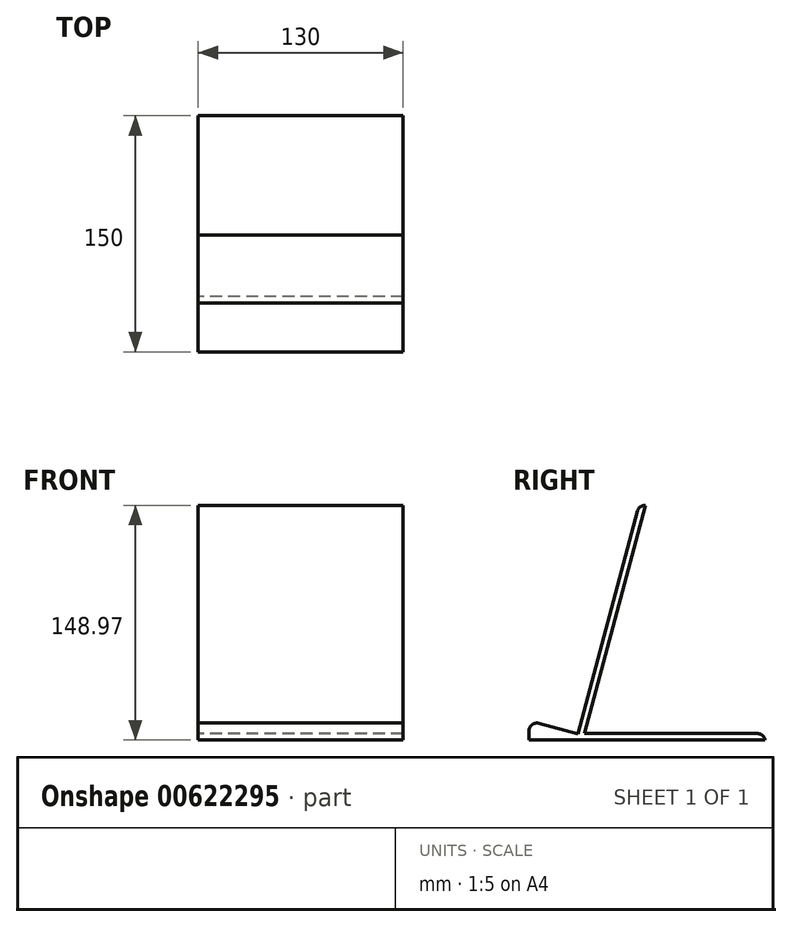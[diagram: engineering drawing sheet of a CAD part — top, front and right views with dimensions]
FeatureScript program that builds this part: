
annotation { "Feature Type Name" : "Feature", "Feature Type Description" : "" }
export const myFeature = defineFeature(function(context is Context, id is Id, definition is map)
    precondition{}
    {
        {
            var Q0;
            Q0=qCreatedBy(makeId("Right.planeOp"),FACE);
            var sketch = newSketch(context, id + "F0", { "sketchPlane" : qUnion([Q0])});
            skLineSegment(sketch, "E0", {"start": v(0, 0) * mm, "end": v(120, 0) * mm});
            skLineSegment(sketch, "E1", {"start": v(120, 0) * mm, "end": v(120, 4) * mm});
            skLineSegment(sketch, "E2", {"start": v(120, 4) * mm, "end": v(5.21, 4) * mm});
            skLineSegment(sketch, "E3", {"start": v(5.21, 4) * mm, "end": v(44.06, 148.96) * mm});
            skLineSegment(sketch, "E4", {"start": v(44.06, 148.96) * mm, "end": v(40.2, 150) * mm});
            skLineSegment(sketch, "E5", {"start": v(40.2, 150) * mm, "end": v(0, 0) * mm});
            skLineSegment(sketch, "E6", {"start": v(0, 0) * mm, "end": v(-30, 0) * mm});
            skLineSegment(sketch, "E7", {"start": v(-30, 0) * mm, "end": v(-30, 4) * mm});
            skLineSegment(sketch, "E8", {"start": v(1.04, 3.86) * mm, "end": v(-30, 12.18) * mm});
            skLineSegment(sketch, "E9", {"start": v(-30, 12.18) * mm, "end": v(-30, 4) * mm});
            skLineSegment(sketch, "E10", {"start": v(1.04, 3.86) * mm, "end": v(0, 0) * mm});
            skSolve(sketch);
        }
        {
            var Q0;
            Q0=makeQuery(id+"F0.imprint","IMPRINT",FACE,{"disambiguationData":[TD([[makeQuery(id+"F0.imprint","IMPRINT",EDGE,{"derivedFrom":sQuery(id+"F0.wireOp",EDGE,"E0")}),1.0]])]});
            var Q1;
            Q1=makeQuery(id+"F0.imprint","IMPRINT",FACE,{"disambiguationData":[TD([[makeQuery(id+"F0.imprint","IMPRINT",EDGE,{"derivedFrom":sQuery(id+"F0.wireOp",EDGE,"E6")}),-1.0]])]});
            extrude(context, id + "F1", {"entities" : qUnion([Q0, Q1]), "depth" : 130 * mm, "offsetDistance" : 25 * mm});
        }
        {
            var Q0;
            Q0=makeQuery(id+"F1.opExtrude","SWEPT_EDGE",EDGE,{"disambiguationData":[OSD([sQuery(id+"F0.wireOp",EDGE,"E4"),sQuery(id+"F0.wireOp",EDGE,"E5")])]});
            fillet(context, id + "F2", {"entities" : qUnion([Q0]), "radius" : 5 * mm, "tangentPropagation" : true, "allowEdgeOverflow" : false});
        }
        {
            var Q0;
            Q0=makeQuery(id+"F1.opExtrude","SWEPT_EDGE",EDGE,{"disambiguationData":[OSD([sQuery(id+"F0.wireOp",EDGE,"E1"),sQuery(id+"F0.wireOp",EDGE,"E2")])]});
            fillet(context, id + "F3", {"entities" : qUnion([Q0]), "radius" : 5 * mm, "tangentPropagation" : true, "allowEdgeOverflow" : false});
        }
        {
            var Q0;
            Q0=makeQuery(id+"F1.opExtrude","SWEPT_EDGE",EDGE,{"disambiguationData":[OSD([sQuery(id+"F0.wireOp",EDGE,"E8"),sQuery(id+"F0.wireOp",EDGE,"E9")])]});
            fillet(context, id + "F4", {"entities" : qUnion([Q0]), "radius" : 5 * mm, "tangentPropagation" : true, "allowEdgeOverflow" : false});
        }
    });
